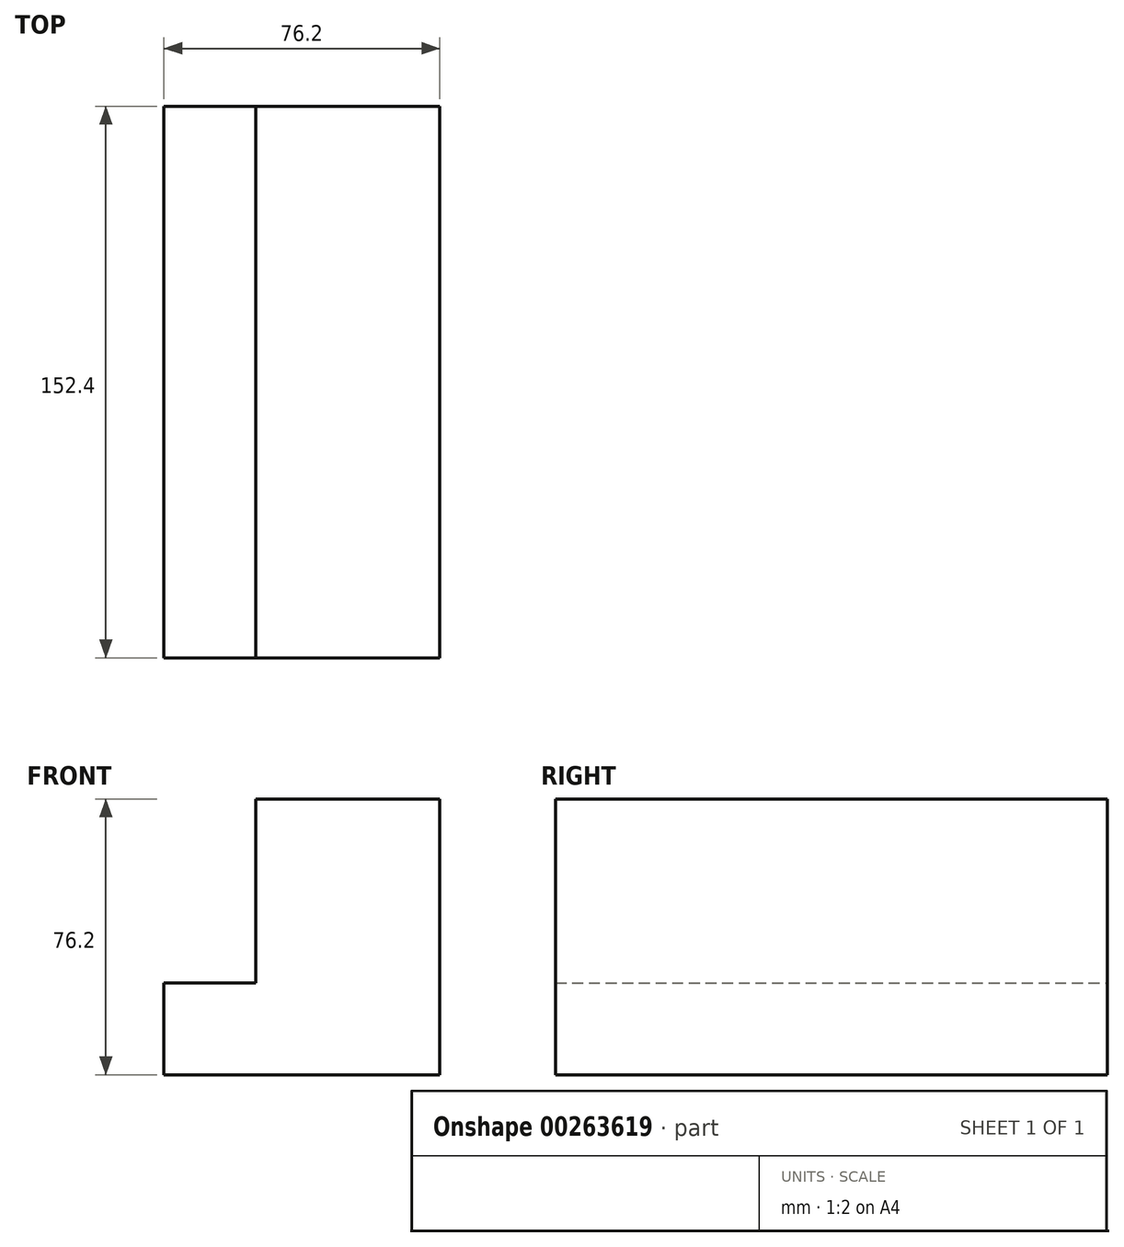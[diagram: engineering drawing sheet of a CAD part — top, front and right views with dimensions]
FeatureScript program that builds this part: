
annotation { "Feature Type Name" : "Feature", "Feature Type Description" : "" }
export const myFeature = defineFeature(function(context is Context, id is Id, definition is map)
    precondition{}
    {
        {
            var Q0;
            Q0=qCreatedBy(makeId("Front.planeOp"),FACE);
            var sketch = newSketch(context, id + "F0", { "sketchPlane" : qUnion([Q0])});
            skLineSegment(sketch, "E0", {"start": v(-76.2, 0) * mm, "end": v(-76.2, 25.4) * mm});
            skLineSegment(sketch, "E1", {"start": v(-76.2, 25.4) * mm, "end": v(-50.8, 25.4) * mm});
            skLineSegment(sketch, "E2", {"start": v(-50.8, 25.4) * mm, "end": v(-50.8, 76.2) * mm});
            skLineSegment(sketch, "E3", {"start": v(-50.8, 76.2) * mm, "end": v(0, 76.2) * mm});
            skLineSegment(sketch, "E4", {"start": v(0, 76.2) * mm, "end": v(0, 0) * mm});
            skLineSegment(sketch, "E5", {"start": v(0, 0) * mm, "end": v(-76.2, 0) * mm});
            skSolve(sketch);
        }
        {
            var Q0;
            Q0=makeQuery(id+"F0.imprint","IMPRINT",FACE,{"disambiguationData":[TD([[makeQuery(id+"F0.imprint","IMPRINT",EDGE,{"derivedFrom":sQuery(id+"F0.wireOp",EDGE,"E0")}),-1.0]])]});
            extrude(context, id + "F1", {"entities" : qUnion([Q0]), "depth" : 152.4 * mm});
        }
    });
